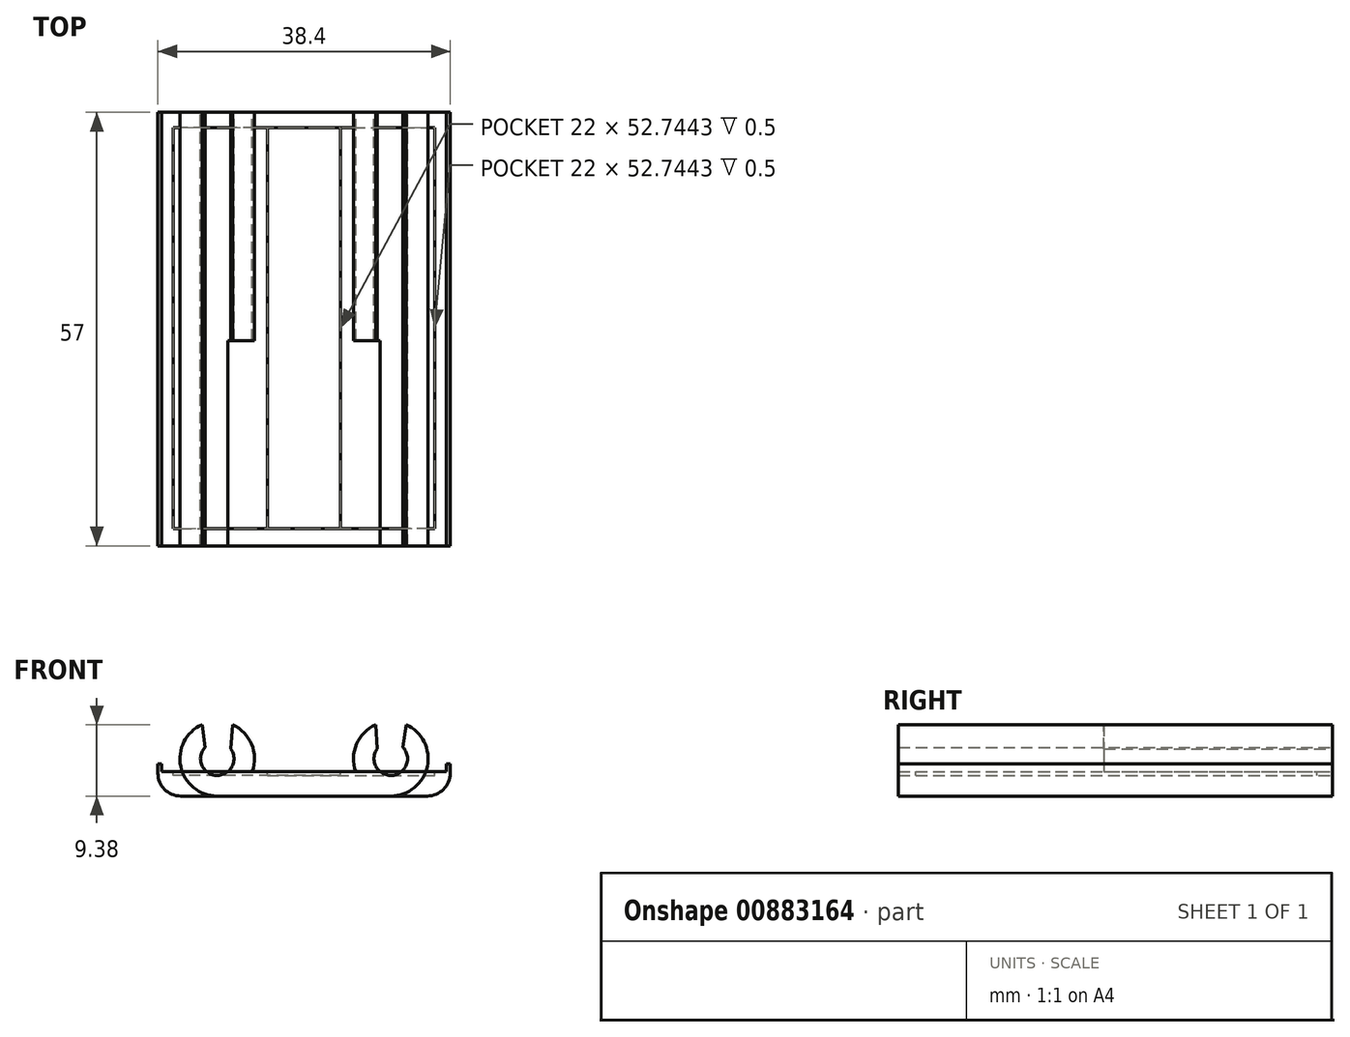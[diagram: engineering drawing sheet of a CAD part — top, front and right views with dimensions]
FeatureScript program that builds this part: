
annotation { "Feature Type Name" : "Feature", "Feature Type Description" : "" }
export const myFeature = defineFeature(function(context is Context, id is Id, definition is map)
    precondition{}
    {
        {
            var Q0;
            Q0=qCreatedBy(makeId("Front.planeOp"),FACE);
            var sketch = newSketch(context, id + "F0", { "sketchPlane" : qUnion([Q0])});
            skLineSegment(sketch, "E0.bottom", {"start": v(-19.2, 1.12) * mm, "end": v(6.8, 1.12) * mm});
            skLineSegment(sketch, "E0.top", {"start": v(-19.2, -2.08) * mm, "end": v(11.4, -2.08) * mm});
            skLineSegment(sketch, "E0.left", {"start": v(-19.2, 1.12) * mm, "end": v(-19.2, -2.08) * mm});
            skArc(sketch, "E1", {"start": v(11.4, -2.08) * mm, "mid": v(16.2, 1.8) * mm, "end": v(13.4, 7.3) * mm});
            skLineSegment(sketch, "E2", {"start": v(16.3, 1.12) * mm, "end": v(16.3, 12.47) * mm, "construction": true});
            skArc(sketch, "E3.0", {"start": v(9.6, 4.1) * mm, "mid": v(11.55, 0.63) * mm, "end": v(13, 4.33) * mm});
            skLineSegment(sketch, "E4", {"start": v(9.6, 4.1) * mm, "end": v(9.4, 7.3) * mm});
            skLineSegment(sketch, "E5", {"start": v(13, 4.33) * mm, "end": v(13.4, 7.3) * mm});
            skArc(sketch, "E6.trimOffspring", {"start": v(9.4, 7.3) * mm, "mid": v(6.88, 4.72) * mm, "end": v(6.8, 1.12) * mm});
            skLineSegment(sketch, "E7", {"start": v(-19.2, 1.12) * mm, "end": v(-19.2, 2.12) * mm});
            skLineSegment(sketch, "E8", {"start": v(-19.2, 2.12) * mm, "end": v(-18.7, 2.12) * mm});
            skLineSegment(sketch, "E9", {"start": v(-18.7, 2.12) * mm, "end": v(-18.7, 1.12) * mm});
            skSolve(sketch);
        }
        {
            var Q0;
            Q0=makeQuery(id+"F0.imprint","IMPRINT",FACE,{"disambiguationData":[TD([[makeQuery(id+"F0.imprint","IMPRINT",EDGE,{"derivedFrom":sQuery(id+"F0.wireOp",EDGE,"E0.bottom")}),-1.0]])]});
            extrude(context, id + "F1", {"entities" : qUnion([Q0]), "depth" : 30 * mm, "offsetDistance" : 25 * mm});
        }
        {
            var Q0;
            Q0=makeQuery(id+"F1.opExtrude","SWEPT_EDGE",EDGE,{"disambiguationData":[OSD([sQuery(id+"F0.wireOp",EDGE,"E0.top"),sQuery(id+"F0.wireOp",EDGE,"E0.left")])]});
            fillet(context, id + "F2", {"entities" : qUnion([Q0]), "radius" : 3 * mm, "tangentPropagation" : true, "allowEdgeOverflow" : false});
        }
        {
            var Q0;
            Q0=makeQuery(id+"F1.opExtrude","CAP_FACE",FACE,{"disambiguationData":[OSD([sQuery(id+"F0.wireOp",EDGE,"E0.bottom"),sQuery(id+"F0.wireOp",EDGE,"E0.top"),sQuery(id+"F0.wireOp",EDGE,"E0.left"),sQuery(id+"F0.wireOp",EDGE,"E1"),sQuery(id+"F0.wireOp",EDGE,"E3.0"),sQuery(id+"F0.wireOp",EDGE,"E4"),sQuery(id+"F0.wireOp",EDGE,"E5"),sQuery(id+"F0.wireOp",EDGE,"E6.trimOffspring")])],"isStart":false});
            var sketch = newSketch(context, id + "F3", { "sketchPlane" : qUnion([Q0])});
            skLineSegment(sketch, "E10", {"start": v(6.8, 1.12) * mm, "end": v(10, 1.12) * mm});
            skSolve(sketch);
        }
        {
            var Q0;
            {var subQ4=sQuery(id+"F3.wireOp",EDGE,"E10");Q0=makeQuery(id+"F3.imprint","IMPRINT",FACE,{"disambiguationData":[TD([[makeQuery(id+"F3.imprint","IMPRINT",EDGE,{"derivedFrom":subQ4}),-1.0]])]});}
            extrude(context, id + "F4", {"entities" : qUnion([Q0]), "operationType" : NewBodyOperationType.ADD, "depth" : 27 * mm, "offsetDistance" : 25 * mm});
        }
        {
            var Q0;
            Q0=makeQuery(id+"F1.opExtrude","SWEPT_FACE",FACE,{"disambiguationData":[OSD([sQuery(id+"F0.wireOp",EDGE,"E0.bottom")])]});
            var sketch = newSketch(context, id + "F5", { "sketchPlane" : qUnion([Q0])});
            skLineSegment(sketch, "E11.0", {"start": v(4.8, -2) * mm, "end": v(-17.2, -2) * mm});
            skLineSegment(sketch, "E11.1", {"start": v(4.8, -54.74) * mm, "end": v(4.8, -2) * mm});
            skLineSegment(sketch, "E11.2", {"start": v(-17.2, -54.74) * mm, "end": v(4.8, -54.74) * mm});
            skLineSegment(sketch, "E11.3", {"start": v(-17.2, -2) * mm, "end": v(-17.2, -54.74) * mm});
            skSolve(sketch);
        }
        {
            var Q0;
            Q0=makeQuery(id+"F5.imprint","IMPRINT",FACE,{"disambiguationData":[TD([[makeQuery(id+"F5.imprint","IMPRINT",EDGE,{"derivedFrom":sQuery(id+"F5.wireOp",EDGE,"dddac458-4b95-48a4-bd78-00d6aba9e8c0.0")}),1.0]])]});
            var Q1;
            Q1=makeQuery(id+"F5.imprint","IMPRINT",FACE,{"disambiguationData":[TD([[makeQuery(id+"F5.imprint","IMPRINT",EDGE,{"derivedFrom":sQuery(id+"F5.wireOp",EDGE,"E11.0")}),1.0]])]});
            extrude(context, id + "F6", {"entities" : qUnion([Q0, Q1]), "operationType" : NewBodyOperationType.REMOVE, "oppositeDirection" : true, "depth" : .5 * mm, "offsetDistance" : 25 * mm});
        }
        {
            var Q0;
            {var subQ0=sQuery(id+"F0.wireOp",EDGE,"E7");Q0=makeQuery(id+"F0.imprint","IMPRINT",FACE,{"disambiguationData":[TD([[makeQuery(id+"F0.imprint","IMPRINT",EDGE,{"derivedFrom":subQ0}),-1.0]])]});}
            extrude(context, id + "F7", {"entities" : qUnion([Q0]), "operationType" : NewBodyOperationType.ADD, "depth" : 57 * mm, "offsetDistance" : 25 * mm});
        }
        {
            var Q0;
            Q0=makeQuery(id+"F1.opExtrude","SWEPT_BODY",BODY,{"disambiguationData":[OSD([sQuery(id+"F0.wireOp",EDGE,"E0.bottom"),sQuery(id+"F0.wireOp",EDGE,"E0.top"),sQuery(id+"F0.wireOp",EDGE,"E0.left"),sQuery(id+"F0.wireOp",EDGE,"E1"),sQuery(id+"F0.wireOp",EDGE,"E3.0"),sQuery(id+"F0.wireOp",EDGE,"E4"),sQuery(id+"F0.wireOp",EDGE,"E5"),sQuery(id+"F0.wireOp",EDGE,"E6.trimOffspring")])]});
            var Q1;
            Q1=qCreatedBy(makeId("Right.planeOp"),FACE);
            mirror(context, id + "F8", {"entities" : qUnion([Q0]), "mirrorPlane" : qUnion([Q1])});
        }
    });
